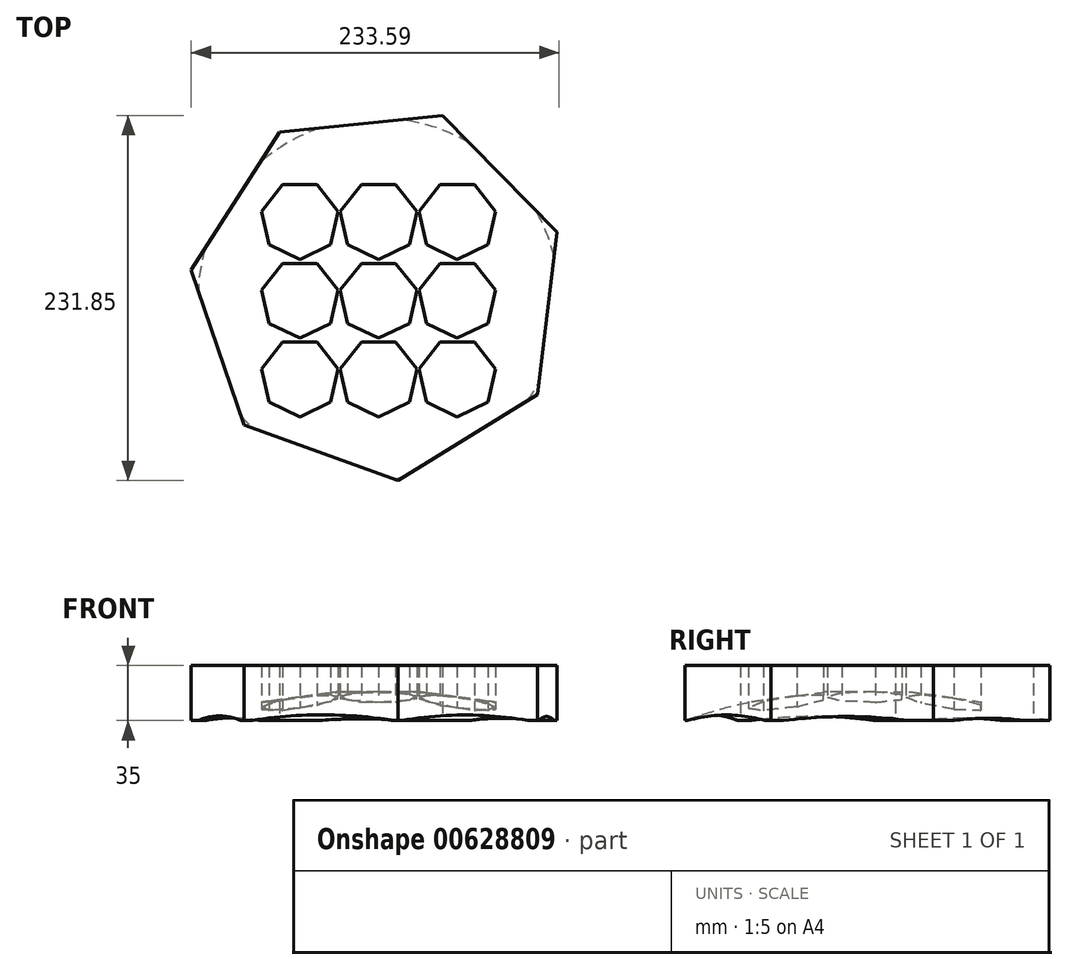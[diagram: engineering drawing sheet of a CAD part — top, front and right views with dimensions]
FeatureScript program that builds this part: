
annotation { "Feature Type Name" : "Feature", "Feature Type Description" : "" }
export const myFeature = defineFeature(function(context is Context, id is Id, definition is map)
    precondition{}
    {
        {
            var Q0;
            Q0=qCreatedBy(makeId("Top.planeOp"),FACE);
            var sketch = newSketch(context, id + "F0", { "sketchPlane" : qUnion([Q0])});
            skCircle(sketch, "E0.cCircle", {"center": v(-50, -50) * mm, "radius": 22.53 * mm, "construction": true});
            skLineSegment(sketch, "E0.0", {"start": v(-60.85, -27.47) * mm, "end": v(-39.15, -27.47) * mm});
            skLineSegment(sketch, "E0.1", {"start": v(-39.15, -27.47) * mm, "end": v(-25.62, -44.44) * mm});
            skLineSegment(sketch, "E0.2", {"start": v(-25.62, -44.44) * mm, "end": v(-30.45, -65.6) * mm});
            skLineSegment(sketch, "E0.3", {"start": v(-30.45, -65.6) * mm, "end": v(-50, -75) * mm});
            skLineSegment(sketch, "E0.4", {"start": v(-50, -75) * mm, "end": v(-69.55, -65.6) * mm});
            skLineSegment(sketch, "E0.5", {"start": v(-69.55, -65.6) * mm, "end": v(-74.38, -44.44) * mm});
            skLineSegment(sketch, "E0.6", {"start": v(-74.38, -44.44) * mm, "end": v(-60.85, -27.47) * mm});
            skPoint(sketch, "E0.0.midPoint", {"position": v(-50, -27.47) * mm});
            skPoint(sketch, "E1.0.1.0", {"position": v(-50, 22.53) * mm});
            skCircle(sketch, "E1.0.1.1", {"center": v(-50, 0) * mm, "radius": 22.53 * mm, "construction": true});
            skLineSegment(sketch, "E1.0.1.2", {"start": v(-60.85, 22.53) * mm, "end": v(-39.15, 22.53) * mm});
            skLineSegment(sketch, "E1.0.1.3", {"start": v(-39.15, 22.53) * mm, "end": v(-25.62, 5.56) * mm});
            skLineSegment(sketch, "E1.0.1.4", {"start": v(-25.62, 5.56) * mm, "end": v(-30.45, -15.6) * mm});
            skLineSegment(sketch, "E1.0.1.5", {"start": v(-30.45, -15.6) * mm, "end": v(-50, -25) * mm});
            skLineSegment(sketch, "E1.0.1.6", {"start": v(-50, -25) * mm, "end": v(-69.55, -15.6) * mm});
            skLineSegment(sketch, "E1.0.1.7", {"start": v(-69.55, -15.6) * mm, "end": v(-74.38, 5.56) * mm});
            skLineSegment(sketch, "E1.0.1.8", {"start": v(-74.38, 5.56) * mm, "end": v(-60.85, 22.53) * mm});
            skPoint(sketch, "E1.0.2.0", {"position": v(-50, 72.53) * mm});
            skCircle(sketch, "E1.0.2.1", {"center": v(-50, 50) * mm, "radius": 22.53 * mm, "construction": true});
            skLineSegment(sketch, "E1.0.2.2", {"start": v(-60.85, 72.53) * mm, "end": v(-39.15, 72.53) * mm});
            skLineSegment(sketch, "E1.0.2.3", {"start": v(-39.15, 72.53) * mm, "end": v(-25.62, 55.56) * mm});
            skLineSegment(sketch, "E1.0.2.4", {"start": v(-25.62, 55.56) * mm, "end": v(-30.45, 34.4) * mm});
            skLineSegment(sketch, "E1.0.2.5", {"start": v(-30.45, 34.4) * mm, "end": v(-50, 25) * mm});
            skLineSegment(sketch, "E1.0.2.6", {"start": v(-50, 25) * mm, "end": v(-69.55, 34.4) * mm});
            skLineSegment(sketch, "E1.0.2.7", {"start": v(-69.55, 34.4) * mm, "end": v(-74.38, 55.56) * mm});
            skLineSegment(sketch, "E1.0.2.8", {"start": v(-74.38, 55.56) * mm, "end": v(-60.85, 72.53) * mm});
            skPoint(sketch, "E1.1.0.0", {"position": v(0, -27.47) * mm});
            skCircle(sketch, "E1.1.0.1", {"center": v(0, -50) * mm, "radius": 22.53 * mm, "construction": true});
            skLineSegment(sketch, "E1.1.0.2", {"start": v(-10.85, -27.47) * mm, "end": v(10.85, -27.47) * mm});
            skLineSegment(sketch, "E1.1.0.3", {"start": v(10.85, -27.47) * mm, "end": v(24.38, -44.44) * mm});
            skLineSegment(sketch, "E1.1.0.4", {"start": v(24.38, -44.44) * mm, "end": v(19.55, -65.6) * mm});
            skLineSegment(sketch, "E1.1.0.5", {"start": v(19.55, -65.6) * mm, "end": v(0, -75) * mm});
            skLineSegment(sketch, "E1.1.0.6", {"start": v(0, -75) * mm, "end": v(-19.55, -65.6) * mm});
            skLineSegment(sketch, "E1.1.0.7", {"start": v(-19.55, -65.6) * mm, "end": v(-24.38, -44.44) * mm});
            skLineSegment(sketch, "E1.1.0.8", {"start": v(-24.38, -44.44) * mm, "end": v(-10.85, -27.47) * mm});
            skPoint(sketch, "E1.1.1.0", {"position": v(0, 22.53) * mm});
            skCircle(sketch, "E1.1.1.1", {"center": v(0, 0) * mm, "radius": 22.53 * mm, "construction": true});
            skLineSegment(sketch, "E1.1.1.2", {"start": v(-10.85, 22.53) * mm, "end": v(10.85, 22.53) * mm});
            skLineSegment(sketch, "E1.1.1.3", {"start": v(10.85, 22.53) * mm, "end": v(24.38, 5.56) * mm});
            skLineSegment(sketch, "E1.1.1.4", {"start": v(24.38, 5.56) * mm, "end": v(19.55, -15.6) * mm});
            skLineSegment(sketch, "E1.1.1.5", {"start": v(19.55, -15.6) * mm, "end": v(0, -25) * mm});
            skLineSegment(sketch, "E1.1.1.6", {"start": v(0, -25) * mm, "end": v(-19.55, -15.6) * mm});
            skLineSegment(sketch, "E1.1.1.7", {"start": v(-19.55, -15.6) * mm, "end": v(-24.38, 5.56) * mm});
            skLineSegment(sketch, "E1.1.1.8", {"start": v(-24.38, 5.56) * mm, "end": v(-10.85, 22.53) * mm});
            skPoint(sketch, "E1.1.2.0", {"position": v(0, 72.53) * mm});
            skCircle(sketch, "E1.1.2.1", {"center": v(0, 50) * mm, "radius": 22.53 * mm, "construction": true});
            skLineSegment(sketch, "E1.1.2.2", {"start": v(-10.85, 72.53) * mm, "end": v(10.85, 72.53) * mm});
            skLineSegment(sketch, "E1.1.2.3", {"start": v(10.85, 72.53) * mm, "end": v(24.38, 55.56) * mm});
            skLineSegment(sketch, "E1.1.2.4", {"start": v(24.38, 55.56) * mm, "end": v(19.55, 34.4) * mm});
            skLineSegment(sketch, "E1.1.2.5", {"start": v(19.55, 34.4) * mm, "end": v(0, 25) * mm});
            skLineSegment(sketch, "E1.1.2.6", {"start": v(0, 25) * mm, "end": v(-19.55, 34.4) * mm});
            skLineSegment(sketch, "E1.1.2.7", {"start": v(-19.55, 34.4) * mm, "end": v(-24.38, 55.56) * mm});
            skLineSegment(sketch, "E1.1.2.8", {"start": v(-24.38, 55.56) * mm, "end": v(-10.85, 72.53) * mm});
            skPoint(sketch, "E1.2.0.0", {"position": v(50, -27.47) * mm});
            skCircle(sketch, "E1.2.0.1", {"center": v(50, -50) * mm, "radius": 22.53 * mm, "construction": true});
            skLineSegment(sketch, "E1.2.0.2", {"start": v(39.15, -27.47) * mm, "end": v(60.85, -27.47) * mm});
            skLineSegment(sketch, "E1.2.0.3", {"start": v(60.85, -27.47) * mm, "end": v(74.38, -44.44) * mm});
            skLineSegment(sketch, "E1.2.0.4", {"start": v(74.38, -44.44) * mm, "end": v(69.55, -65.6) * mm});
            skLineSegment(sketch, "E1.2.0.5", {"start": v(69.55, -65.6) * mm, "end": v(50, -75) * mm});
            skLineSegment(sketch, "E1.2.0.6", {"start": v(50, -75) * mm, "end": v(30.45, -65.6) * mm});
            skLineSegment(sketch, "E1.2.0.7", {"start": v(30.45, -65.6) * mm, "end": v(25.62, -44.44) * mm});
            skLineSegment(sketch, "E1.2.0.8", {"start": v(25.62, -44.44) * mm, "end": v(39.15, -27.47) * mm});
            skPoint(sketch, "E1.2.1.0", {"position": v(50, 22.53) * mm});
            skCircle(sketch, "E1.2.1.1", {"center": v(50, 0) * mm, "radius": 22.53 * mm, "construction": true});
            skLineSegment(sketch, "E1.2.1.2", {"start": v(39.15, 22.53) * mm, "end": v(60.85, 22.53) * mm});
            skLineSegment(sketch, "E1.2.1.3", {"start": v(60.85, 22.53) * mm, "end": v(74.38, 5.56) * mm});
            skLineSegment(sketch, "E1.2.1.4", {"start": v(74.38, 5.56) * mm, "end": v(69.55, -15.6) * mm});
            skLineSegment(sketch, "E1.2.1.5", {"start": v(69.55, -15.6) * mm, "end": v(50, -25) * mm});
            skLineSegment(sketch, "E1.2.1.6", {"start": v(50, -25) * mm, "end": v(30.45, -15.6) * mm});
            skLineSegment(sketch, "E1.2.1.7", {"start": v(30.45, -15.6) * mm, "end": v(25.62, 5.56) * mm});
            skLineSegment(sketch, "E1.2.1.8", {"start": v(25.62, 5.56) * mm, "end": v(39.15, 22.53) * mm});
            skPoint(sketch, "E1.2.2.0", {"position": v(50, 72.53) * mm});
            skCircle(sketch, "E1.2.2.1", {"center": v(50, 50) * mm, "radius": 22.53 * mm, "construction": true});
            skLineSegment(sketch, "E1.2.2.2", {"start": v(39.15, 72.53) * mm, "end": v(60.85, 72.53) * mm});
            skLineSegment(sketch, "E1.2.2.3", {"start": v(60.85, 72.53) * mm, "end": v(74.38, 55.56) * mm});
            skLineSegment(sketch, "E1.2.2.4", {"start": v(74.38, 55.56) * mm, "end": v(69.55, 34.4) * mm});
            skLineSegment(sketch, "E1.2.2.5", {"start": v(69.55, 34.4) * mm, "end": v(50, 25) * mm});
            skLineSegment(sketch, "E1.2.2.6", {"start": v(50, 25) * mm, "end": v(30.45, 34.4) * mm});
            skLineSegment(sketch, "E1.2.2.7", {"start": v(30.45, 34.4) * mm, "end": v(25.62, 55.56) * mm});
            skLineSegment(sketch, "E1.2.2.8", {"start": v(25.62, 55.56) * mm, "end": v(39.15, 72.53) * mm});
            skLineSegment(sketch, "E1.direction1", {"start": v(-69.55, -65.6) * mm, "end": v(-19.55, -65.6) * mm, "construction": true});
            skLineSegment(sketch, "E1.direction2", {"start": v(-69.55, -65.6) * mm, "end": v(-69.55, -15.6) * mm, "construction": true});
            skCircle(sketch, "E2.cCircle", {"center": v(0, 3.8) * mm, "radius": 107.92 * mm, "construction": true});
            skLineSegment(sketch, "E2.0", {"start": v(40.57, 116.5) * mm, "end": v(113.41, 42.35) * mm});
            skLineSegment(sketch, "E2.1", {"start": v(113.41, 42.35) * mm, "end": v(100.85, -60.83) * mm});
            skLineSegment(sketch, "E2.2", {"start": v(100.85, -60.83) * mm, "end": v(12.35, -115.34) * mm});
            skLineSegment(sketch, "E2.3", {"start": v(12.35, -115.34) * mm, "end": v(-85.46, -80.13) * mm});
            skLineSegment(sketch, "E2.4", {"start": v(-85.46, -80.13) * mm, "end": v(-118.9, 18.28) * mm});
            skLineSegment(sketch, "E2.5", {"start": v(-118.9, 18.28) * mm, "end": v(-62.82, 105.8) * mm});
            skLineSegment(sketch, "E2.6", {"start": v(-62.82, 105.8) * mm, "end": v(40.57, 116.5) * mm});
            skPoint(sketch, "E2.0.midPoint", {"position": v(77, 79.43) * mm});
            skSolve(sketch);
        }
        {
            var Q0;
            Q0=makeQuery(id+"F0.imprint","IMPRINT",FACE,{"disambiguationData":[TD([[makeQuery(id+"F0.imprint","IMPRINT",EDGE,{"derivedFrom":sQuery(id+"F0.wireOp",EDGE,"E0.0")}),1.0]])]});
            var Q1;
            Q1 = qSketchRegion(id + "F2", true);
            extrude(context, id + "F1", {"entities" : qUnion([Q0, Q1]), "depth" : 35 * mm, "offsetDistance" : 25 * mm});
        }
        {
            var Q0;
            Q0=qCreatedBy(makeId("Right.planeOp"),FACE);
            var sketch = newSketch(context, id + "F2", { "sketchPlane" : qUnion([Q0])});
            skEllipticalArc(sketch, "E3", {});
            skLineSegment(sketch, "E4", {"start": v(-115.35, -0.25) * mm, "end": v(0, -0.47) * mm});
            skLineSegment(sketch, "E5", {"start": v(0, 18.95) * mm, "end": v(0, -0.47) * mm});
            skPoint(sketch, "E6.orphan", {"position": v(0, 50.27) * mm});
            const initialGuessF2  = {"E3": [0, -0.07563124597072601, -1, 0, 0.19097839295864105, 0.09458022203011182, 4.71238898038469, 5.360874539212009]};
            skSetInitialGuess(sketch, initialGuessF2);
            skSolve(sketch);
        }
        {
            var Q0;
            Q0=qCreatedBy(makeId("Right.planeOp"),FACE);
            var sketch = newSketch(context, id + "F3", { "sketchPlane" : qUnion([Q0])});
            skLineSegment(sketch, "E7", {"start": v(0, 80.37) * mm, "end": v(0, -96.48) * mm, "construction": true});
            skSolve(sketch);
        }
        {
            var Q0;
            Q0=makeQuery(id+"F2.imprint","IMPRINT",FACE,{"disambiguationData":[TD([[makeQuery(id+"F2.imprint","IMPRINT",EDGE,{"derivedFrom":sQuery(id+"F2.wireOp",EDGE,"E3")}),1.0]])]});
            var Q1;
            Q1=sQuery(id+"F3.wireOp",EDGE,"E7");
            revolve(context, id + "F4", {"operationType" : NewBodyOperationType.REMOVE, "entities" : qUnion([Q0]), "axis" : qUnion([Q1]), "revolveType" : RevolveType.FULL});
        }
    });
